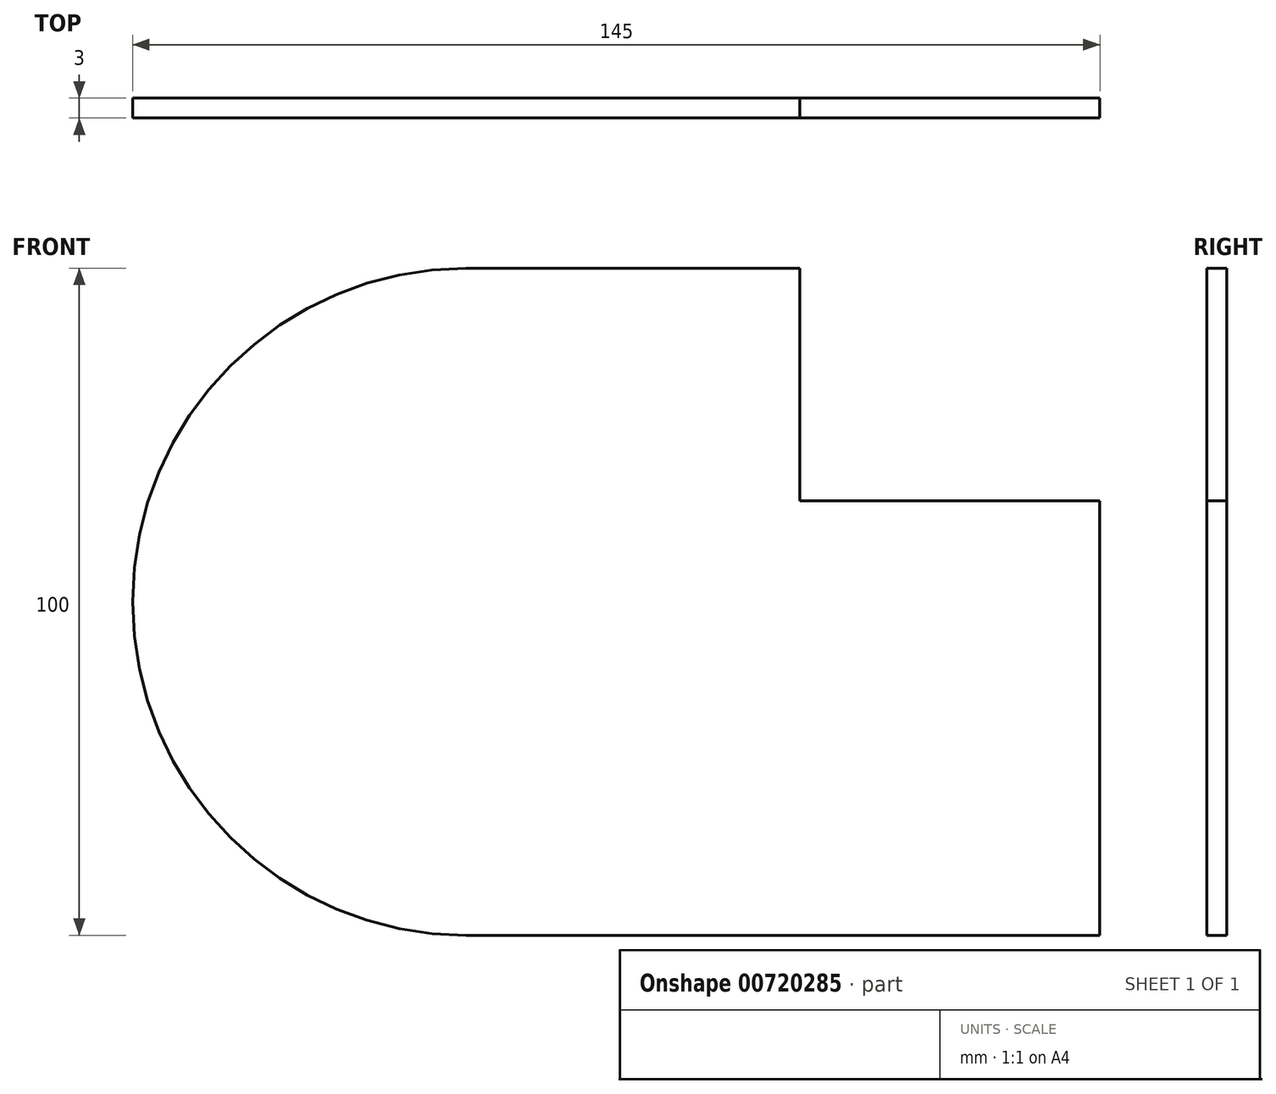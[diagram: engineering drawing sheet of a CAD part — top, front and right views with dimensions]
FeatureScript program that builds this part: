
annotation { "Feature Type Name" : "Feature", "Feature Type Description" : "" }
export const myFeature = defineFeature(function(context is Context, id is Id, definition is map)
    precondition{}
    {
        {
            var Q0;
            Q0=qCreatedBy(makeId("Front.planeOp"),FACE);
            var sketch = newSketch(context, id + "F0", { "sketchPlane" : qUnion([Q0])});
            skArc(sketch, "E0", {"start": v(-124.1, 57.97) * mm, "mid": v(-174.1, 7.97) * mm, "end": v(-124.1, -42.03) * mm});
            skLineSegment(sketch, "E1", {"start": v(-124.1, 57.97) * mm, "end": v(-74.1, 57.97) * mm});
            skLineSegment(sketch, "E2", {"start": v(-124.1, -42.03) * mm, "end": v(-29.1, -42.03) * mm});
            skLineSegment(sketch, "E3", {"start": v(-29.1, -42.03) * mm, "end": v(-29.1, 23.11) * mm});
            skPoint(sketch, "E4.end.orphan", {"position": v(-174.1, 7.97) * mm});
            skLineSegment(sketch, "E5", {"start": v(-29.1, 23.11) * mm, "end": v(-74.1, 23.11) * mm});
            skLineSegment(sketch, "E6", {"start": v(-74.1, 23.11) * mm, "end": v(-74.1, 58.11) * mm});
            skPoint(sketch, "E7.start.orphan", {"position": v(-29.1, 7.97) * mm});
            skLineSegment(sketch, "E8.trimOffspring", {"start": v(-29.1, 57.97) * mm, "end": v(-29.1, 58.11) * mm});
            skSolve(sketch);
        }
        {
            var Q0;
            Q0 = qSketchRegion(id + "F0", true);
            extrude(context, id + "F1", {"entities" : qUnion([Q0]), "depth" : 3 * mm, "offsetDistance" : 25 * mm});
        }
    });
